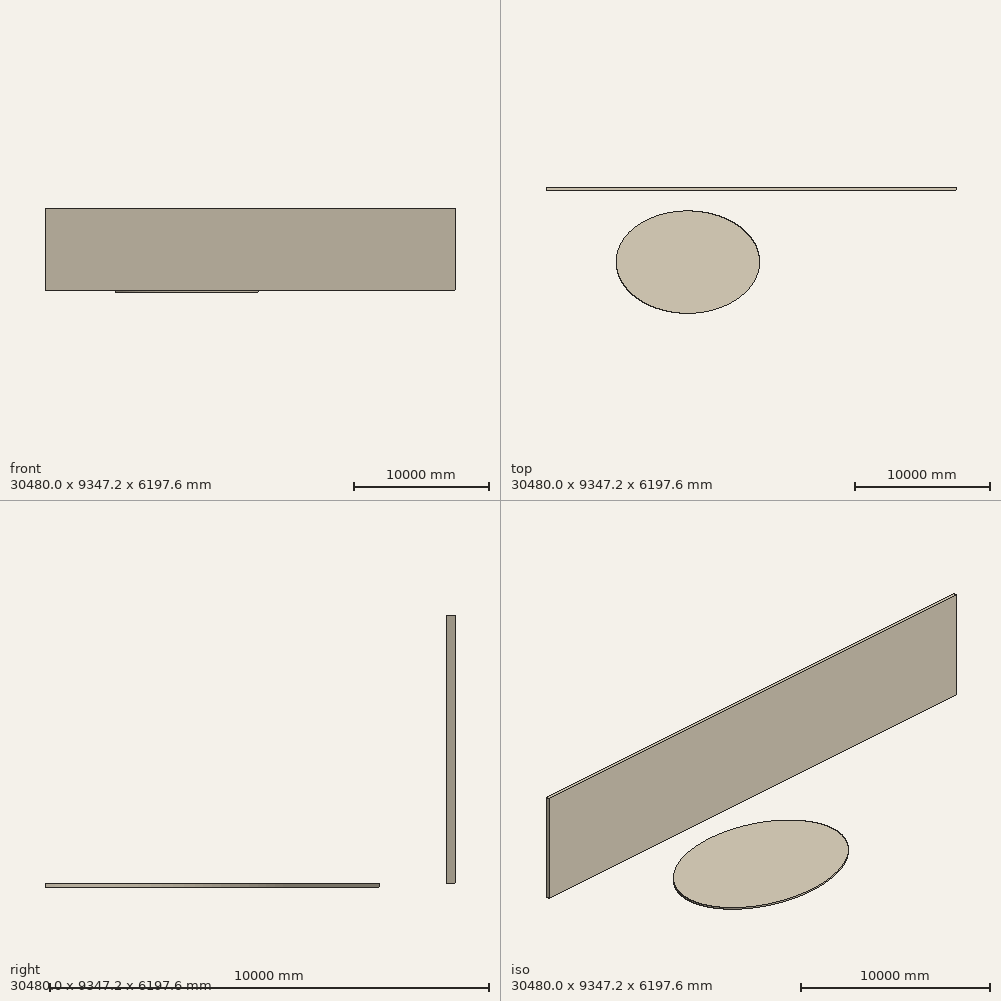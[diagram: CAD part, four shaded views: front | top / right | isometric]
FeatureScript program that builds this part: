
annotation { "Feature Type Name" : "Feature", "Feature Type Description" : "" }
export const myFeature = defineFeature(function(context is Context, id is Id, definition is map)
    precondition{}
    {
        {
            var Q0;
            Q0=qCreatedBy(makeId("Top.planeOp"),FACE);
            var sketch = newSketch(context, id + "F0", { "sketchPlane" : qUnion([Q0])});
            skEllipse(sketch, "E0", {"center": v(0, 0) * mm, "majorRadius": 5334 * mm, "minorRadius": 3810 * mm, "majorAxis": v(1, 0)});
            skFitSpline(sketch, "E1.0", {"points": [v(6857.97, -18.46) * mm, v(6858.01, 0) * mm, v(6857.97, 18.46) * mm, v(6857.81, 43.07) * mm, v(6857.41, 73.81) * mm, v(6856.61, 110.68) * mm, v(6855.12, 159.8) * mm, v(6852.46, 221.11) * mm, v(6848, 294.55) * mm, v(6842.27, 367.82) * mm, v(6832.96, 465.27) * mm, v(6818.2, 586.57) * mm, v(6795.57, 731.15) * mm, v(6758.94, 922.46) * mm, v(6701.23, 1158.47) * mm, v(6613.63, 1435.72) * mm, v(6508.5, 1706.15) * mm, v(6386.62, 1969.09) * mm, v(6248.85, 2223.96) * mm, v(6095.96, 2470.32) * mm, v(5928.7, 2707.84) * mm, v(5747.8, 2936.25) * mm, v(5586.22, 3118.83) * mm, v(5450.74, 3260.16) * mm, v(5346.1, 3363.77) * mm, v(5238.49, 3464.98) * mm, v(5127.97, 3563.79) * mm, v(5033.5, 3644.1) * mm, v(4956.52, 3707.13) * mm, v(4898.1, 3753.8) * mm, v(4838.99, 3799.85) * mm, v(4789.17, 3837.71) * mm, v(4748.98, 3867.7) * mm, v(4718.66, 3890.03) * mm, v(4693.27, 3908.51) * mm, v(4672.86, 3923.22) * mm, v(4657.52, 3934.21) * mm, v(4642.14, 3945.17) * mm, v(4621.6, 3959.7) * mm, v(4595.83, 3977.77) * mm, v(4564.78, 3999.27) * mm, v(4523.23, 4027.7) * mm, v(4470.97, 4062.77) * mm, v(4407.77, 4104.15) * mm, v(4344.1, 4144.82) * mm, v(4258.59, 4198.1) * mm, v(4150.54, 4262.93) * mm, v(4019.12, 4337.93) * mm, v(3886, 4410.13) * mm, v(3751.24, 4479.56) * mm, v(3569.45, 4568.45) * mm, v(3338.4, 4672.72) * mm, v(3055.5, 4786.97) * mm, v(2767.34, 4890.43) * mm, v(2474.35, 4983.14) * mm, v(2176.88, 5065.13) * mm, v(1875.33, 5136.39) * mm, v(1570.04, 5196.9) * mm, v(1312.82, 5238.34) * mm, v(1105.54, 5266.05) * mm, v(949.38, 5284.1) * mm, v(792.55, 5299.43) * mm, v(635.1, 5312) * mm, v(503.42, 5320.17) * mm, v(397.82, 5325.31) * mm, v(318.48, 5328.48) * mm, v(239.03, 5330.94) * mm, v(172.73, 5332.41) * mm, v(119.63, 5333.23) * mm, v(79.78, 5333.68) * mm, v(46.55, 5333.9) * mm, v(19.95, 5333.99) * mm, v(0, 5334) * mm, v(-19.95, 5333.99) * mm, v(-46.55, 5333.9) * mm, v(-79.78, 5333.68) * mm, v(-119.63, 5333.23) * mm, v(-172.73, 5332.41) * mm, v(-239.03, 5330.94) * mm, v(-318.48, 5328.48) * mm, v(-397.82, 5325.31) * mm, v(-503.42, 5320.17) * mm, v(-635.1, 5312) * mm, v(-792.55, 5299.43) * mm, v(-949.38, 5284.1) * mm, v(-1105.54, 5266.05) * mm, v(-1312.82, 5238.34) * mm, v(-1570.04, 5196.9) * mm, v(-1875.33, 5136.39) * mm, v(-2176.88, 5065.13) * mm, v(-2474.35, 4983.14) * mm, v(-2767.34, 4890.43) * mm, v(-3055.5, 4786.97) * mm, v(-3338.4, 4672.72) * mm, v(-3569.45, 4568.45) * mm, v(-3751.24, 4479.56) * mm, v(-3886, 4410.13) * mm, v(-4019.12, 4337.93) * mm, v(-4150.54, 4262.93) * mm, v(-4258.59, 4198.1) * mm, v(-4344.1, 4144.82) * mm, v(-4407.77, 4104.15) * mm, v(-4470.97, 4062.77) * mm, v(-4523.23, 4027.7) * mm, v(-4564.78, 3999.27) * mm, v(-4595.83, 3977.77) * mm, v(-4621.6, 3959.7) * mm, v(-4642.14, 3945.17) * mm, v(-4657.52, 3934.21) * mm, v(-4672.86, 3923.22) * mm, v(-4693.27, 3908.51) * mm, v(-4718.66, 3890.03) * mm, v(-4748.98, 3867.7) * mm, v(-4789.17, 3837.71) * mm, v(-4838.99, 3799.85) * mm, v(-4898.1, 3753.8) * mm, v(-4956.52, 3707.13) * mm, v(-5033.5, 3644.1) * mm, v(-5127.97, 3563.79) * mm, v(-5238.49, 3464.98) * mm, v(-5346.1, 3363.77) * mm, v(-5450.74, 3260.16) * mm, v(-5586.22, 3118.83) * mm, v(-5747.8, 2936.25) * mm, v(-5928.7, 2707.84) * mm, v(-6095.96, 2470.32) * mm, v(-6248.85, 2223.96) * mm, v(-6386.62, 1969.09) * mm, v(-6508.5, 1706.15) * mm, v(-6613.63, 1435.72) * mm, v(-6701.23, 1158.47) * mm, v(-6758.94, 922.46) * mm, v(-6795.57, 731.15) * mm, v(-6818.2, 586.57) * mm, v(-6832.96, 465.27) * mm, v(-6842.27, 367.82) * mm, v(-6848, 294.55) * mm, v(-6852.46, 221.11) * mm, v(-6855.12, 159.8) * mm, v(-6856.61, 110.68) * mm, v(-6857.41, 73.81) * mm, v(-6857.81, 43.07) * mm, v(-6857.97, 18.46) * mm, v(-6858.01, 0) * mm, v(-6857.97, -18.46) * mm, v(-6857.81, -43.07) * mm, v(-6857.41, -73.81) * mm, v(-6856.61, -110.68) * mm, v(-6855.12, -159.8) * mm, v(-6852.46, -221.11) * mm, v(-6848, -294.55) * mm, v(-6842.27, -367.82) * mm, v(-6832.96, -465.27) * mm, v(-6818.2, -586.57) * mm, v(-6795.57, -731.15) * mm, v(-6758.94, -922.46) * mm, v(-6701.23, -1158.47) * mm, v(-6613.63, -1435.72) * mm, v(-6508.5, -1706.15) * mm, v(-6386.62, -1969.09) * mm, v(-6248.85, -2223.96) * mm, v(-6095.96, -2470.32) * mm, v(-5928.7, -2707.84) * mm, v(-5747.8, -2936.25) * mm, v(-5586.22, -3118.83) * mm, v(-5450.74, -3260.16) * mm, v(-5346.1, -3363.77) * mm, v(-5238.49, -3464.98) * mm, v(-5127.97, -3563.79) * mm, v(-5033.5, -3644.1) * mm, v(-4956.52, -3707.13) * mm, v(-4898.1, -3753.8) * mm, v(-4838.99, -3799.85) * mm, v(-4789.17, -3837.71) * mm, v(-4748.98, -3867.7) * mm, v(-4718.66, -3890.03) * mm, v(-4693.27, -3908.51) * mm, v(-4672.86, -3923.22) * mm, v(-4657.52, -3934.21) * mm, v(-4642.14, -3945.17) * mm, v(-4621.6, -3959.7) * mm, v(-4595.83, -3977.77) * mm, v(-4564.78, -3999.27) * mm, v(-4523.23, -4027.7) * mm, v(-4470.97, -4062.77) * mm, v(-4407.77, -4104.15) * mm, v(-4344.1, -4144.82) * mm, v(-4258.59, -4198.1) * mm, v(-4150.54, -4262.93) * mm, v(-4019.12, -4337.93) * mm, v(-3886, -4410.13) * mm, v(-3751.24, -4479.56) * mm, v(-3569.45, -4568.45) * mm, v(-3338.4, -4672.72) * mm, v(-3055.5, -4786.97) * mm, v(-2767.34, -4890.43) * mm, v(-2474.35, -4983.14) * mm, v(-2176.88, -5065.13) * mm, v(-1875.33, -5136.39) * mm, v(-1570.04, -5196.9) * mm, v(-1312.82, -5238.34) * mm, v(-1105.54, -5266.05) * mm, v(-949.38, -5284.1) * mm, v(-792.55, -5299.43) * mm, v(-635.1, -5312) * mm, v(-503.42, -5320.17) * mm, v(-397.82, -5325.31) * mm, v(-318.48, -5328.48) * mm, v(-239.03, -5330.94) * mm, v(-172.73, -5332.41) * mm, v(-119.63, -5333.23) * mm, v(-79.78, -5333.68) * mm, v(-46.55, -5333.9) * mm, v(-19.95, -5333.99) * mm, v(0, -5334) * mm, v(19.95, -5333.99) * mm, v(46.55, -5333.9) * mm, v(79.78, -5333.68) * mm, v(119.63, -5333.23) * mm, v(172.73, -5332.41) * mm, v(239.03, -5330.94) * mm, v(318.48, -5328.48) * mm, v(397.82, -5325.31) * mm, v(503.42, -5320.17) * mm, v(635.1, -5312) * mm, v(792.55, -5299.43) * mm, v(949.38, -5284.1) * mm, v(1105.54, -5266.05) * mm, v(1312.82, -5238.34) * mm, v(1570.04, -5196.9) * mm, v(1875.33, -5136.39) * mm, v(2176.88, -5065.13) * mm, v(2474.35, -4983.14) * mm, v(2767.34, -4890.43) * mm, v(3055.5, -4786.97) * mm, v(3338.4, -4672.72) * mm, v(3569.45, -4568.45) * mm, v(3751.24, -4479.56) * mm, v(3886, -4410.13) * mm, v(4019.12, -4337.93) * mm, v(4150.54, -4262.93) * mm, v(4258.59, -4198.1) * mm, v(4344.1, -4144.82) * mm, v(4407.77, -4104.15) * mm, v(4470.97, -4062.77) * mm, v(4523.23, -4027.7) * mm, v(4564.78, -3999.27) * mm, v(4595.83, -3977.77) * mm, v(4621.6, -3959.7) * mm, v(4642.14, -3945.17) * mm, v(4657.52, -3934.21) * mm, v(4672.86, -3923.22) * mm, v(4693.27, -3908.51) * mm, v(4718.66, -3890.03) * mm, v(4748.98, -3867.7) * mm, v(4789.17, -3837.71) * mm, v(4838.99, -3799.85) * mm, v(4898.1, -3753.8) * mm, v(4956.52, -3707.13) * mm, v(5033.5, -3644.1) * mm, v(5127.97, -3563.79) * mm, v(5238.49, -3464.98) * mm, v(5346.1, -3363.77) * mm, v(5450.74, -3260.16) * mm, v(5586.22, -3118.83) * mm, v(5747.8, -2936.25) * mm, v(5928.7, -2707.84) * mm, v(6095.96, -2470.32) * mm, v(6248.85, -2223.96) * mm, v(6386.62, -1969.09) * mm, v(6508.5, -1706.15) * mm, v(6613.63, -1435.72) * mm, v(6701.23, -1158.47) * mm, v(6758.94, -922.46) * mm, v(6795.57, -731.15) * mm, v(6818.2, -586.57) * mm, v(6832.96, -465.27) * mm, v(6842.27, -367.82) * mm, v(6848, -294.55) * mm, v(6852.46, -221.11) * mm, v(6855.12, -159.8) * mm, v(6856.61, -110.68) * mm, v(6857.41, -73.81) * mm, v(6857.81, -43.07) * mm, v(6857.97, -18.46) * mm, v(6858.01, 0) * mm, v(6857.97, 18.46) * mm]});
            skLineSegment(sketch, "E2.bottom", {"start": v(6858, 5334) * mm, "end": v(-6858, 5334) * mm});
            skLineSegment(sketch, "E2.top", {"start": v(6858, 0) * mm, "end": v(-6858, 0) * mm, "construction": true});
            skLineSegment(sketch, "E2.left", {"start": v(6858, 5334) * mm, "end": v(6858, 0) * mm});
            skLineSegment(sketch, "E2.right", {"start": v(-6858, 5334) * mm, "end": v(-6858, 0) * mm});
            skPoint(sketch, "E2.middle", {"position": v(0, 2667) * mm});
            skSolve(sketch);
        }
        {
            var Q0;
            Q0 = qSketchRegion(id + "F0", true);
            extrude(context, id + "F1", {"entities" : qUnion([Q0]), "oppositeDirection" : true, "depth" : 101.6 * mm, "offsetDistance" : 25.4 * mm});
        }
        {
            var Q0;
            Q0=qCreatedBy(makeId("Top.planeOp"),FACE);
            var sketch = newSketch(context, id + "F2", { "sketchPlane" : qUnion([Q0])});
            skLineSegment(sketch, "E3.bottom", {"start": v(-10515.6, 5334) * mm, "end": v(19964.4, 5334) * mm});
            skLineSegment(sketch, "E3.top", {"start": v(-10515.6, 5537.2) * mm, "end": v(19964.4, 5537.2) * mm});
            skLineSegment(sketch, "E3.left", {"start": v(-10515.6, 5334) * mm, "end": v(-10515.6, 5537.2) * mm});
            skLineSegment(sketch, "E3.right", {"start": v(19964.4, 5334) * mm, "end": v(19964.4, 5537.2) * mm});
            skSolve(sketch);
        }
        {
            var Q0;
            Q0 = qSketchRegion(id + "F2", true);
            extrude(context, id + "F3", {"entities" : qUnion([Q0]), "depth" : 6096 * mm, "offsetDistance" : 25.4 * mm});
        }
    });
